# Revit family: Gira_028228
name_source: partatom
category: Electrical Fixtures
revit_build: Autodesk Revit 2017 (Build: 20160225_1515(x64)
units: mm (PartAtom-declared; Revit-internal decimal feet)

## family parameters
Cut with Voids When Loaded = No
Host = Face
Maintain Annotation Orientation = No
Part Type = Normal
Room Calculation Point = No
Round Connector Dimension = Use Diameter
Shared = No

## types (1)
- Adapterrahmen quadr. 50 x 50 mm System 55 Anthrazit
    Abmessungen = quadratisch 50 mm / quadratisch 50 mm
    Abschließbar = No
    Available = Yes
    Category = Übergangsadapter für Installationsschalterprogramme
    Data sheet (1) = https://katalog.gira.de
    Default Elevation = 1219 mm
    Farbe = anthrazit
    GTIN = 4010337282280
    HAN = 028228
    HeinzeBIM = https://bimportal.heinze.de
    Keynote = Sys55_Adapterrahmen_50x50
    Manufacturer URL = https://www.gira.de
    Mit Klappdeckel = No
    Mit Textfeld = No
    Name = Adapterrahmen quadr. 50 x 50 mm System 55 Anthrazit
    Region = DE
    URL = http://katalog.gira.de

## geometry (parser evidence)
native form markers: Blend x2, Sweep x3
no freeform markers — native parametric forms only
